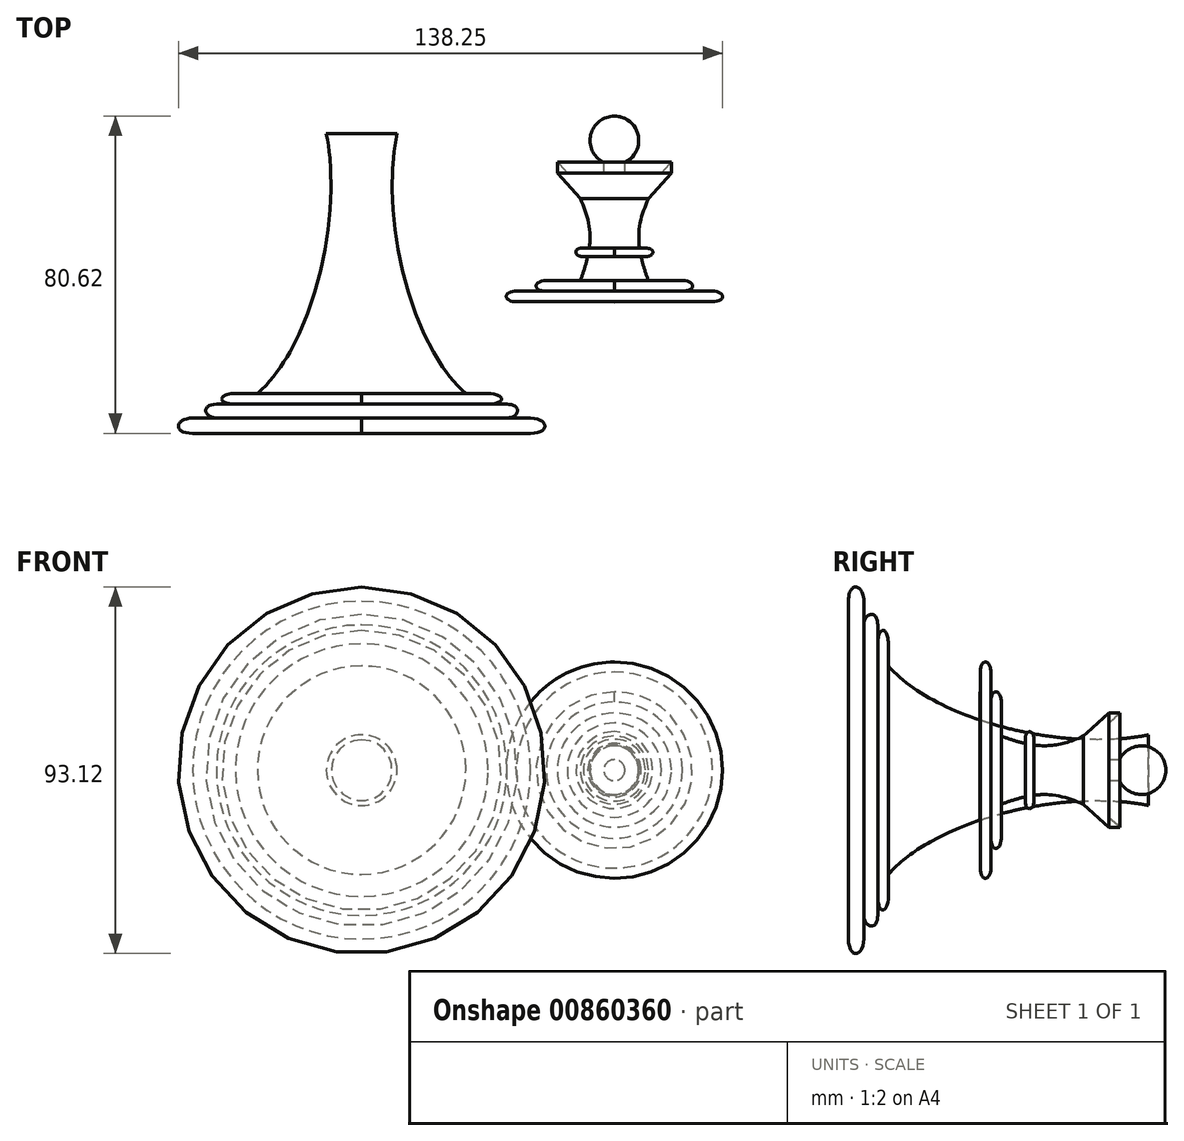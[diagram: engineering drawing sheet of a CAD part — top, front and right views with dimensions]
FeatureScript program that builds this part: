
annotation { "Feature Type Name" : "Feature", "Feature Type Description" : "" }
export const myFeature = defineFeature(function(context is Context, id is Id, definition is map)
    precondition{}
    {
        {
            var Q0;
            Q0=qCreatedBy(makeId("Top.planeOp"),FACE);
            var sketch = newSketch(context, id + "F0", { "sketchPlane" : qUnion([Q0])});
            skFitSpline(sketch, "E0", {"points": [v(8.98, 38.44) * mm, v(26.48, -27.6) * mm], "startDerivative": vector(-13.57, -65.2) * mm, "endDerivative": vector(41.02, -35.33) * mm});
            skLineSegment(sketch, "E1", {"start": v(0, -27.6) * mm, "end": v(32.08, -27.6) * mm});
            skLineSegment(sketch, "E2", {"start": v(32.08, -30.33) * mm, "end": v(36.9, -30.33) * mm});
            skLineSegment(sketch, "E3", {"start": v(36.9, -33.85) * mm, "end": v(42.92, -33.85) * mm});
            skLineSegment(sketch, "E4", {"start": v(42.92, -37.76) * mm, "end": v(0, -37.76) * mm});
            skLineSegment(sketch, "E5", {"start": v(0, 44.9) * mm, "end": v(0, -37.76) * mm});
            skFitSpline(sketch, "E6", {"points": [v(32.08, -27.6) * mm, v(32.08, -30.33) * mm], "startDerivative": vector(13.07, -0.13) * mm, "endDerivative": vector(-14.45, 0) * mm});
            skFitSpline(sketch, "E7", {"points": [v(36.9, -30.33) * mm, v(36.9, -33.85) * mm], "startDerivative": vector(12.42, -0.26) * mm, "endDerivative": vector(-9.03, 0) * mm});
            skFitSpline(sketch, "E8", {"points": [v(42.92, -33.85) * mm, v(42.92, -37.76) * mm], "startDerivative": vector(13.7, -0.19) * mm, "endDerivative": vector(-15.36, 0.06) * mm});
            skLineSegment(sketch, "E9", {"start": v(8.98, 38.44) * mm, "end": v(0, 38.44) * mm});
            skLineSegment(sketch, "E10", {"start": v(64.2, 28.4) * mm, "end": v(78.7, 28.4) * mm});
            skLineSegment(sketch, "E11", {"start": v(64.2, 21.96) * mm, "end": v(72.86, 21.96) * mm});
            skLineSegment(sketch, "E12", {"start": v(78.7, 28.4) * mm, "end": v(72.86, 21.96) * mm});
            skFitSpline(sketch, "E13", {"points": [v(72.86, 21.96) * mm, v(72.86, 1.06) * mm], "startDerivative": vector(-10.46, -23.63) * mm, "endDerivative": vector(9.14, -24.9) * mm});
            skLineSegment(sketch, "E14", {"start": v(64.2, 9.3) * mm, "end": v(72.08, 9.35) * mm});
            skLineSegment(sketch, "E15", {"start": v(72.08, 7.19) * mm, "end": v(64.2, 7.04) * mm});
            skLineSegment(sketch, "E16", {"start": v(64.2, 1.06) * mm, "end": v(81.5, 1.06) * mm});
            skLineSegment(sketch, "E17", {"start": v(81.5, -1.6) * mm, "end": v(89.1, -1.6) * mm});
            skLineSegment(sketch, "E18", {"start": v(89.1, -4.29) * mm, "end": v(64.2, -4.37) * mm});
            skLineSegment(sketch, "E19", {"start": v(66.87, 32.6) * mm, "end": v(66.87, 28.4) * mm});
            skArc(sketch, "E20", {"start": v(64.2, 30.49) * mm, "mid": v(70.4, 36.68) * mm, "end": v(64.2, 42.86) * mm});
            skLineSegment(sketch, "E21", {"start": v(78.7, 28.4) * mm, "end": v(78.7, 31.19) * mm});
            skLineSegment(sketch, "E22", {"start": v(78.7, 31.19) * mm, "end": v(76.17, 28.4) * mm});
            skFitSpline(sketch, "E23", {"points": [v(72.08, 9.35) * mm, v(72.08, 7.19) * mm], "startDerivative": vector(7.9, 0) * mm, "endDerivative": vector(-7.43, 0.46) * mm});
            skFitSpline(sketch, "E24", {"points": [v(81.5, 1.06) * mm, v(81.5, -1.6) * mm], "startDerivative": vector(9.36, 0.04) * mm, "endDerivative": vector(-11.4, 0) * mm});
            skFitSpline(sketch, "E25", {"points": [v(89.1, -1.6) * mm, v(89.1, -4.29) * mm], "startDerivative": vector(10.34, -0.3) * mm, "endDerivative": vector(-10.34, -0.05) * mm});
            skLineSegment(sketch, "E26", {"start": v(64.2, 42.86) * mm, "end": v(64.2, -4.37) * mm});
            skSolve(sketch);
        }
        {
            var Q0;
            {var subQ0=sQuery(id+"F0.wireOp",EDGE,"E0");Q0=makeQuery(id+"F0.imprint","IMPRINT",FACE,{"disambiguationData":[TD([[makeQuery(id+"F0.imprint","IMPRINT",EDGE,{"derivedFrom":subQ0}),-1.0]])]});}
            var Q1;
            Q1=makeQuery(id+"F0.imprint","IMPRINT",FACE,{"disambiguationData":[TD([[makeQuery(id+"F0.imprint","IMPRINT",EDGE,{"derivedFrom":sQuery(id+"F0.wireOp",EDGE,"E2")}),-1.0]])]});
            var Q2;
            Q2=sQuery(id+"F0.wireOp",EDGE,"E5");
            revolve(context, id + "F1", {"surfaceOperationType" : NewSurfaceOperationType.NEW, "entities" : qUnion([Q0, Q1]), "axis" : qUnion([Q2]), "revolveType" : RevolveType.FULL});
        }
        {
            var Q0;
            {var subQ0=sQuery(id+"F0.wireOp",EDGE,"E21");Q0=makeQuery(id+"F0.imprint","IMPRINT",FACE,{"disambiguationData":[TD([[makeQuery(id+"F0.imprint","IMPRINT",EDGE,{"derivedFrom":subQ0}),1.0]])]});}
            var Q1;
            Q1=makeQuery(id+"F0.imprint","IMPRINT",FACE,{"disambiguationData":[TD([[makeQuery(id+"F0.imprint","IMPRINT",EDGE,{"derivedFrom":sQuery(id+"F0.wireOp",EDGE,"E17")}),-1.0]])]});
            var Q2;
            {var subQ0=sQuery(id+"F0.wireOp",EDGE,"E14");var subQ1=sQuery(id+"F0.wireOp",EDGE,"E13");var subQ2=makeQuery(id+"F0.imprint","INTERSECT",VERTEX,{"derivedFrom":[subQ1,subQ0]});Q2=makeQuery(id+"F0.imprint","IMPRINT",FACE,{"disambiguationData":[TD([[makeQuery(id+"F0.imprint","IMPRINT",EDGE,{"disambiguationData":[TD([[subQ2,-1.0]])],"derivedFrom":subQ1}),-1.0]])]});}
            var Q3;
            {var subQ0=sQuery(id+"F0.wireOp",EDGE,"E26");var subQ1=sQuery(id+"F0.wireOp",EDGE,"E10");var subQ2=makeQuery(id+"F0.imprint","INTERSECT",VERTEX,{"derivedFrom":[subQ1,subQ0]});Q3=makeQuery(id+"F0.imprint","IMPRINT",FACE,{"disambiguationData":[TD([[makeQuery(id+"F0.imprint","IMPRINT",EDGE,{"disambiguationData":[TD([[subQ2,-1.0]])],"derivedFrom":subQ1}),1.0]])]});}
            var Q4;
            {var subQ5=sQuery(id+"F0.wireOp",EDGE,"E23");Q4=makeQuery(id+"F0.imprint","IMPRINT",FACE,{"disambiguationData":[TD([[makeQuery(id+"F0.imprint","IMPRINT",EDGE,{"derivedFrom":subQ5}),-1.0]])]});}
            var Q5;
            {var subQ0=sQuery(id+"F0.wireOp",EDGE,"E16");var subQ1=sQuery(id+"F0.wireOp",EDGE,"E13");var subQ2=makeQuery(id+"F0.imprint","INTERSECT",VERTEX,{"derivedFrom":[subQ1,subQ0]});Q5=makeQuery(id+"F0.imprint","IMPRINT",FACE,{"disambiguationData":[TD([[makeQuery(id+"F0.imprint","IMPRINT",EDGE,{"disambiguationData":[TD([[subQ2,1.0]])],"derivedFrom":subQ1}),-1.0]])]});}
            var Q6;
            {var subQ0=sQuery(id+"F0.wireOp",EDGE,"E11");Q6=makeQuery(id+"F0.imprint","IMPRINT",FACE,{"disambiguationData":[TD([[makeQuery(id+"F0.imprint","IMPRINT",EDGE,{"derivedFrom":subQ0}),1.0]])]});}
            var Q7;
            {var subQ0=sQuery(id+"F0.wireOp",EDGE,"E26");var subQ1=sQuery(id+"F0.wireOp",EDGE,"E20");var subQ2=makeQuery(id+"F0.imprint","INTERSECT",VERTEX,{"disambiguationData":[OD(0.0)],"derivedFrom":[subQ1,subQ0]});Q7=makeQuery(id+"F0.imprint","IMPRINT",FACE,{"disambiguationData":[TD([[makeQuery(id+"F0.imprint","IMPRINT",EDGE,{"disambiguationData":[TD([[subQ2,-1.0]])],"derivedFrom":subQ1}),1.0]])]});}
            var Q8;
            {var subQ0=sQuery(id+"F0.wireOp",EDGE,"E11");Q8=makeQuery(id+"F0.imprint","IMPRINT",FACE,{"disambiguationData":[TD([[makeQuery(id+"F0.imprint","IMPRINT",EDGE,{"derivedFrom":subQ0}),-1.0]])]});}
            var Q9;
            Q9=sQuery(id+"F0.wireOp",EDGE,"E26");
            revolve(context, id + "F2", {"surfaceOperationType" : NewSurfaceOperationType.NEW, "entities" : qUnion([Q0, Q1, Q2, Q3, Q4, Q5, Q6, Q7, Q8]), "axis" : qUnion([Q9]), "revolveType" : RevolveType.FULL});
        }
    });
